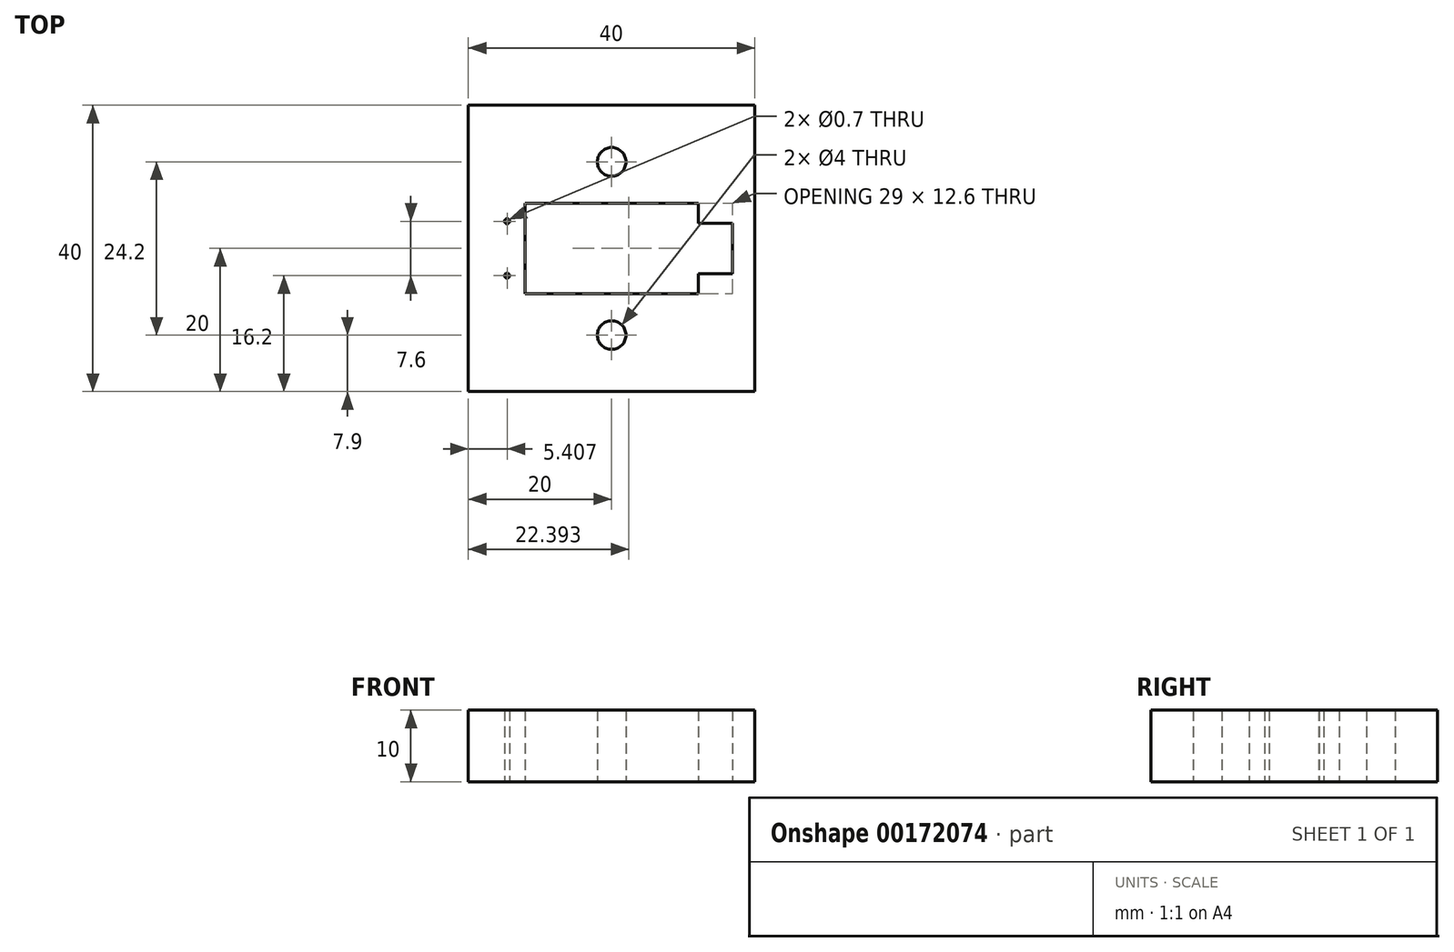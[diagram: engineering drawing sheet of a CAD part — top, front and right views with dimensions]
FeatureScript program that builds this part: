
annotation { "Feature Type Name" : "Feature", "Feature Type Description" : "" }
export const myFeature = defineFeature(function(context is Context, id is Id, definition is map)
    precondition{}
    {
        {
            var Q0;
            Q0=qCreatedBy(makeId("Top.planeOp"),FACE);
            var sketch = newSketch(context, id + "F0", { "sketchPlane" : qUnion([Q0])});
            skLineSegment(sketch, "E0.bottom", {"start": v(0, 0) * mm, "end": v(40, 0) * mm});
            skLineSegment(sketch, "E0.top", {"start": v(0, 40) * mm, "end": v(40, 40) * mm});
            skLineSegment(sketch, "E0.left", {"start": v(0, 0) * mm, "end": v(0, 40) * mm});
            skLineSegment(sketch, "E0.right", {"start": v(40, 0) * mm, "end": v(40, 40) * mm});
            skCircle(sketch, "E1", {"center": v(20, 32.1) * mm, "radius": 2 * mm});
            skCircle(sketch, "E2", {"center": v(20, 7.9) * mm, "radius": 2 * mm});
            skLineSegment(sketch, "E3.bottom", {"start": v(7.9, 26.3) * mm, "end": v(32.1, 26.3) * mm});
            skLineSegment(sketch, "E3.top", {"start": v(7.9, 13.7) * mm, "end": v(32.1, 13.7) * mm});
            skLineSegment(sketch, "E3.left", {"start": v(7.9, 26.3) * mm, "end": v(7.9, 13.7) * mm});
            skLineSegment(sketch, "E3.right", {"start": v(32.1, 26.3) * mm, "end": v(32.1, 23.5) * mm});
            skLineSegment(sketch, "E4", {"start": v(20, 32.1) * mm, "end": v(20, 40) * mm, "construction": true});
            skLineSegment(sketch, "E5", {"start": v(20, 7.9) * mm, "end": v(20, 0) * mm, "construction": true});
            skLineSegment(sketch, "E6", {"start": v(20, 0) * mm, "end": v(20, 40) * mm, "construction": true});
            skLineSegment(sketch, "E7", {"start": v(20, 26.3) * mm, "end": v(20, 13.7) * mm, "construction": true});
            skLineSegment(sketch, "E8", {"start": v(7.9, 20) * mm, "end": v(32.1, 20) * mm, "construction": true});
            skLineSegment(sketch, "E9", {"start": v(0, 20) * mm, "end": v(40, 20) * mm, "construction": true});
            skLineSegment(sketch, "E10.bottom", {"start": v(32.1, 23.5) * mm, "end": v(36.9, 23.5) * mm});
            skLineSegment(sketch, "E10.top", {"start": v(32.1, 16.5) * mm, "end": v(36.9, 16.5) * mm});
            skLineSegment(sketch, "E10.right", {"start": v(36.9, 23.5) * mm, "end": v(36.9, 16.5) * mm});
            skLineSegment(sketch, "E11", {"start": v(36.9, 20) * mm, "end": v(32.1, 20) * mm, "construction": true});
            skLineSegment(sketch, "E12.trimOffspring", {"start": v(32.1, 16.5) * mm, "end": v(32.1, 13.7) * mm});
            skLineSegment(sketch, "E13", {"start": v(5.4, 23.8) * mm, "end": v(5.4, 16.2) * mm, "construction": true});
            skCircle(sketch, "E14", {"center": v(5.4, 23.8) * mm, "radius": 0.35 * mm});
            skCircle(sketch, "E15", {"center": v(5.4, 16.2) * mm, "radius": 0.35 * mm});
            skSolve(sketch);
        }
        {
            var Q0;
            Q0=qSketchRegion(id+"F0",true);
            extrude(context, id + "F1", {"entities" : qUnion([Q0]), "depth" : 10 * mm});
        }
    });
